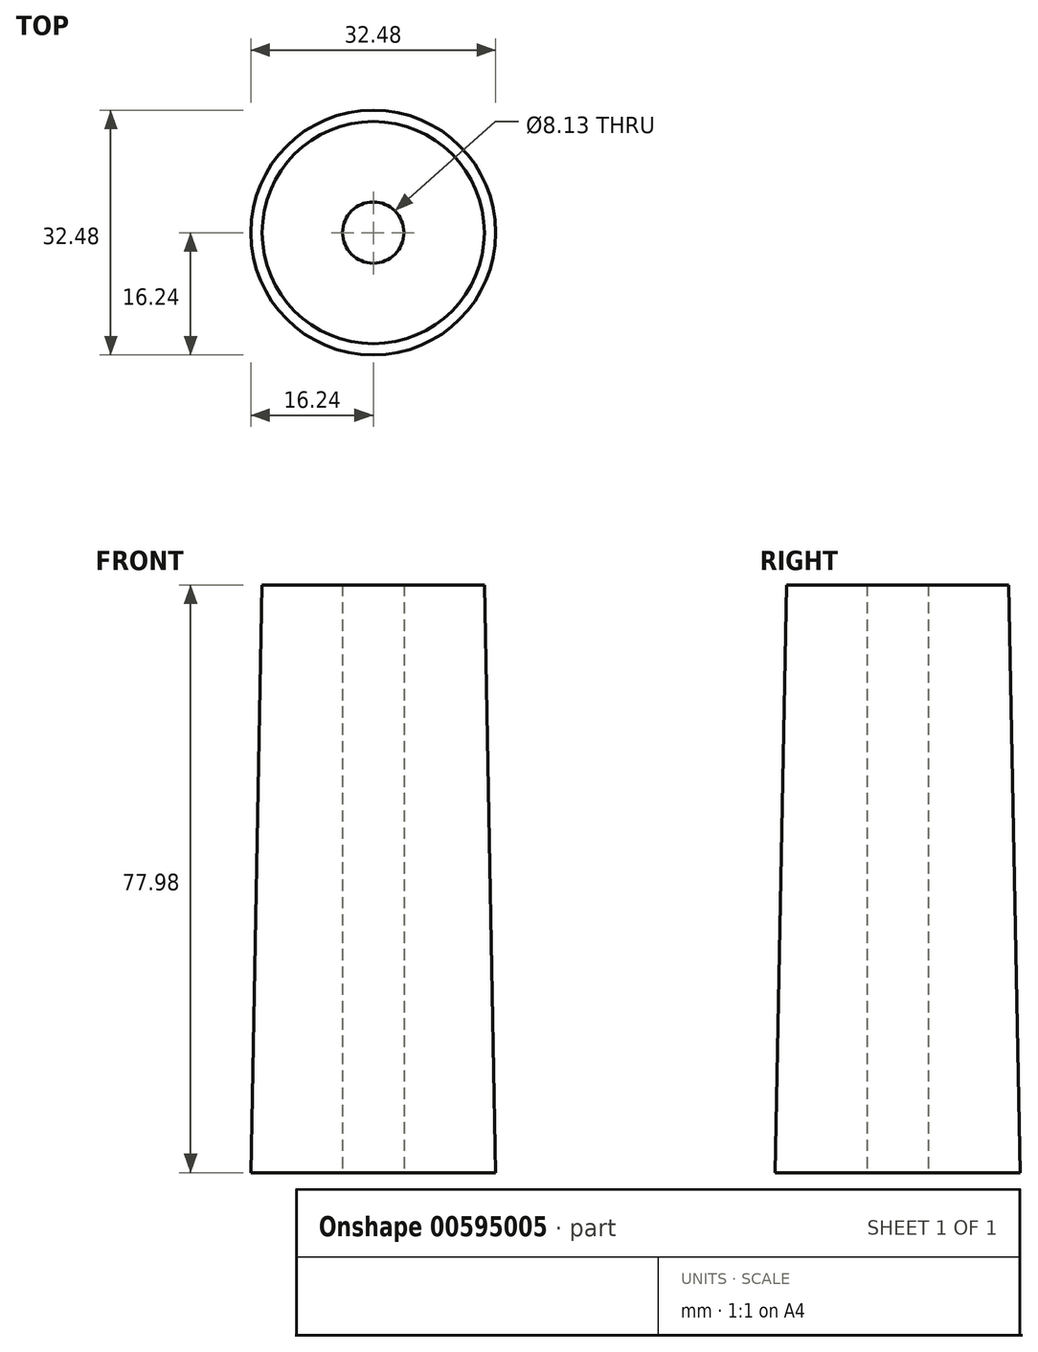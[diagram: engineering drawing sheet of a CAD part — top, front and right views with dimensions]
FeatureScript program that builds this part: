
annotation { "Feature Type Name" : "Feature", "Feature Type Description" : "" }
export const myFeature = defineFeature(function(context is Context, id is Id, definition is map)
    precondition{}
    {
        {
            var Q0;
            Q0=qCreatedBy(makeId("Top.planeOp"),FACE);
            var sketch = newSketch(context, id + "F0", { "sketchPlane" : qUnion([Q0])});
            skCircle(sketch, "E0", {"center": v(0, 0) * mm, "radius": 16.24 * mm});
            skSolve(sketch);
        }
        {
            var Q0;
            Q0=makeQuery(id+"F0.imprint","IMPRINT",FACE,{"disambiguationData":[TD([[makeQuery(id+"F0.imprint","IMPRINT",EDGE,{"derivedFrom":sQuery(id+"F0.wireOp",EDGE,"E0")}),1.0]])]});
            cPlane(context, id + "F1", {"entities" : qUnion([Q0]), "cplaneType" : CPlaneType.OFFSET, "offset" : 77.98 * mm, "width" : 152.4 * mm, "height" : 152.4 * mm});
        }
        {
            var Q0;
            Q0=qCreatedBy(id+"F1.planeOp",FACE);
            var sketch = newSketch(context, id + "F2", { "sketchPlane" : qUnion([Q0])});
            skCircle(sketch, "E1", {"center": v(0, 0) * mm, "radius": 14.74 * mm});
            skSolve(sketch);
        }
        {
            var Q0;
            Q0=makeQuery(id+"F2.imprint","IMPRINT",FACE,{"disambiguationData":[TD([[makeQuery(id+"F2.imprint","IMPRINT",EDGE,{"derivedFrom":sQuery(id+"F2.wireOp",EDGE,"E1")}),1.0]])]});
            var Q1;
            Q1=makeQuery(id+"F0.imprint","IMPRINT",FACE,{"disambiguationData":[TD([[makeQuery(id+"F0.imprint","IMPRINT",EDGE,{"derivedFrom":sQuery(id+"F0.wireOp",EDGE,"E0")}),1.0]])]});
            loft(context, id + "F3", {"sheetProfilesArray" : [{ "sheetProfileEntities" : qUnion([Q0]) }, { "sheetProfileEntities" : qUnion([Q1]) }]});
        }
        {
            var Q0;
            Q0=sQuery(id+"F0.wireOp",VERTEX,"E0.center");
            var Q1;
            Q1=makeQuery(id+"F3.opLoft","SWEPT_BODY",BODY,{"disambiguationData":[OSD([makeQuery(id+"F0.imprint","IMPRINT",FACE,{"disambiguationData":[TD([[makeQuery(id+"F0.imprint","IMPRINT",EDGE,{"derivedFrom":sQuery(id+"F0.wireOp",EDGE,"E0")}),1.0]])]}),makeQuery(id+"F2.imprint","IMPRINT",FACE,{"disambiguationData":[TD([[makeQuery(id+"F2.imprint","IMPRINT",EDGE,{"derivedFrom":sQuery(id+"F2.wireOp",EDGE,"E1")}),1.0]])]})])]});
            hole(context, id + "F4", {"style" : HoleStyle.SIMPLE, "endStyle" : HoleEndStyle.THROUGH, "oppositeDirection" : true, "holeDiameter" : 8.13 * mm, "majorDiameter" : 6.35 * mm, "isTappedThrough" : true, "tappedDepth" : 12.7 * mm, "tapClearance" : 3, "locations" : qUnion([Q0]), "scope" : qUnion([Q1])});
        }
    });
